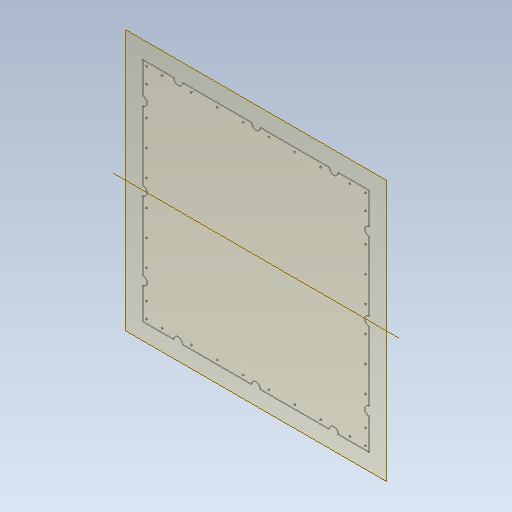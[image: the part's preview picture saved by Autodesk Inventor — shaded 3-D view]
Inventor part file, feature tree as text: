
AUTODESK INVENTOR PART (.ipt)
format: ipt  version: 2021 (Build 250183000, 183)  size: 225,792 bytes
history: native  units: mm
features: other x6, sketch x1, extrude x1, reference x1
ambient origin geometry x8: Origin, YZ Plane, XZ Plane, XY Plane, X Axis, Y Axis, Z Axis, Center Point
bodies: Body1 (feature_tree)
feature tree (9):
  other  "Bryła1"
  other  "Płaszczyzna konstrukcyjna1"
  sketch  "Szkic1"
  other  "Oś konstrukcyjna1"
  extrude  "Wyciągnięcie proste1"  Depth=875.0mm
  reference  "Odniesienie1"
  parser-record x1  (decoder bookkeeping rows leaked as tree rows — omitted from the tree; the rows remain in map.json)
  other  "zespolokno.iam"
  other  "alu:1"
note: 1 file-system path scrubbed to <path> (originals preserved in map.json)
